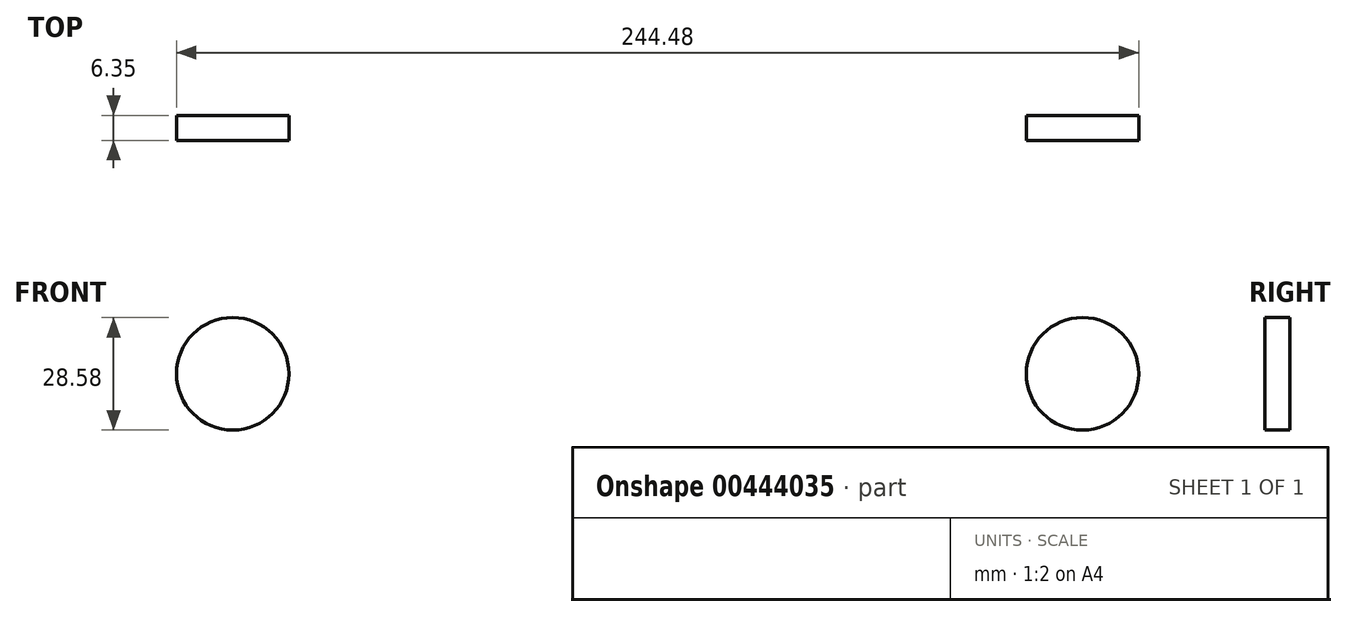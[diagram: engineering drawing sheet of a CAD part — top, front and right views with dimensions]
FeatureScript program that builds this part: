
annotation { "Feature Type Name" : "Feature", "Feature Type Description" : "" }
export const myFeature = defineFeature(function(context is Context, id is Id, definition is map)
    precondition{}
    {
        {
            var Q0;
            Q0=qCreatedBy(makeId("Front.planeOp"),FACE);
            var sketch = newSketch(context, id + "F0", { "sketchPlane" : qUnion([Q0])});
            skLineSegment(sketch, "E0.bottom", {"start": v(215.9, 41.28) * mm, "end": v(-215.9, 41.28) * mm});
            skLineSegment(sketch, "E0.top", {"start": v(215.9, -41.28) * mm, "end": v(-215.9, -41.28) * mm});
            skLineSegment(sketch, "E0.left", {"start": v(215.9, 41.28) * mm, "end": v(215.9, -41.28) * mm});
            skLineSegment(sketch, "E0.right", {"start": v(-215.9, 41.28) * mm, "end": v(-215.9, -41.28) * mm});
            skPoint(sketch, "E0.middle", {"position": v(0, 0) * mm});
            skSolve(sketch);
        }
        {
            var Q0;
            Q0=makeQuery(id+"F0.imprint","IMPRINT",FACE,{"disambiguationData":[TD([[makeQuery(id+"F0.imprint","IMPRINT",EDGE,{"derivedFrom":sQuery(id+"F0.wireOp",EDGE,"E0.bottom")}),1.0]])]});
            extrude(context, id + "F1", {"entities" : qUnion([Q0]), "depth" : 6.35 * mm});
        }
        {
            var Q0;
            Q0=makeQuery(id+"F1.opExtrude","CAP_FACE",FACE,{"disambiguationData":[OSD([sQuery(id+"F0.wireOp",EDGE,"E0.bottom"),sQuery(id+"F0.wireOp",EDGE,"E0.top"),sQuery(id+"F0.wireOp",EDGE,"E0.left"),sQuery(id+"F0.wireOp",EDGE,"E0.right")])],"isStart":false});
            var sketch = newSketch(context, id + "F2", { "sketchPlane" : qUnion([Q0])});
            skLineSegment(sketch, "E1", {"start": v(-215.9, 0) * mm, "end": v(215.9, 0) * mm});
            skCircle(sketch, "E2", {"center": v(107.95, 0) * mm, "radius": 14.29 * mm});
            skCircle(sketch, "E3", {"center": v(-107.95, 0) * mm, "radius": 14.29 * mm});
            skCircle(sketch, "E4", {"center": v(0, 0) * mm, "radius": 14.29 * mm});
            skSolve(sketch);
        }
        {
            var Q0;
            {var subQ0=sQuery(id+"F2.wireOp",EDGE,"E3");var subQ1=sQuery(id+"F2.wireOp",EDGE,"E1");var subQ2=makeQuery(id+"F2.imprint","INTERSECT",VERTEX,{"disambiguationData":[OD(0.0)],"derivedFrom":[subQ1,subQ0]});Q0=makeQuery(id+"F2.imprint","IMPRINT",FACE,{"disambiguationData":[TD([[makeQuery(id+"F2.imprint","IMPRINT",EDGE,{"disambiguationData":[TD([[subQ2,-1.0]])],"derivedFrom":subQ1}),1.0]])]});}
            var Q1;
            {var subQ0=sQuery(id+"F2.wireOp",EDGE,"E3");var subQ1=sQuery(id+"F2.wireOp",EDGE,"E1");var subQ2=makeQuery(id+"F2.imprint","INTERSECT",VERTEX,{"disambiguationData":[OD(0.0)],"derivedFrom":[subQ1,subQ0]});Q1=makeQuery(id+"F2.imprint","IMPRINT",FACE,{"disambiguationData":[TD([[makeQuery(id+"F2.imprint","IMPRINT",EDGE,{"disambiguationData":[TD([[subQ2,-1.0]])],"derivedFrom":subQ1}),-1.0]])]});}
            var Q2;
            {var subQ0=sQuery(id+"F2.wireOp",EDGE,"E4");var subQ1=sQuery(id+"F2.wireOp",EDGE,"E1");var subQ2=makeQuery(id+"F2.imprint","INTERSECT",VERTEX,{"disambiguationData":[OD(0.0)],"derivedFrom":[subQ1,subQ0]});Q2=makeQuery(id+"F2.imprint","IMPRINT",FACE,{"disambiguationData":[TD([[makeQuery(id+"F2.imprint","IMPRINT",EDGE,{"disambiguationData":[TD([[subQ2,-1.0]])],"derivedFrom":subQ1}),-1.0]])]});}
            var Q3;
            {var subQ0=sQuery(id+"F2.wireOp",EDGE,"E4");var subQ1=sQuery(id+"F2.wireOp",EDGE,"E1");var subQ2=makeQuery(id+"F2.imprint","INTERSECT",VERTEX,{"disambiguationData":[OD(0.0)],"derivedFrom":[subQ1,subQ0]});Q3=makeQuery(id+"F2.imprint","IMPRINT",FACE,{"disambiguationData":[TD([[makeQuery(id+"F2.imprint","IMPRINT",EDGE,{"disambiguationData":[TD([[subQ2,-1.0]])],"derivedFrom":subQ1}),1.0]])]});}
            var Q4;
            {var subQ0=sQuery(id+"F2.wireOp",EDGE,"E2");var subQ1=sQuery(id+"F2.wireOp",EDGE,"E1");var subQ2=makeQuery(id+"F2.imprint","INTERSECT",VERTEX,{"disambiguationData":[OD(0.0)],"derivedFrom":[subQ1,subQ0]});Q4=makeQuery(id+"F2.imprint","IMPRINT",FACE,{"disambiguationData":[TD([[makeQuery(id+"F2.imprint","IMPRINT",EDGE,{"disambiguationData":[TD([[subQ2,-1.0]])],"derivedFrom":subQ1}),-1.0]])]});}
            var Q5;
            {var subQ0=sQuery(id+"F2.wireOp",EDGE,"E2");var subQ1=sQuery(id+"F2.wireOp",EDGE,"E1");var subQ2=makeQuery(id+"F2.imprint","INTERSECT",VERTEX,{"disambiguationData":[OD(0.0)],"derivedFrom":[subQ1,subQ0]});Q5=makeQuery(id+"F2.imprint","IMPRINT",FACE,{"disambiguationData":[TD([[makeQuery(id+"F2.imprint","IMPRINT",EDGE,{"disambiguationData":[TD([[subQ2,-1.0]])],"derivedFrom":subQ1}),1.0]])]});}
            var Q6;
            Q6=makeQuery(id+"F1.opExtrude","CAP_FACE",FACE,{"disambiguationData":[OSD([sQuery(id+"F0.wireOp",EDGE,"E0.bottom"),sQuery(id+"F0.wireOp",EDGE,"E0.top"),sQuery(id+"F0.wireOp",EDGE,"E0.left"),sQuery(id+"F0.wireOp",EDGE,"E0.right")])],"isStart":true});
            extrude(context, id + "F3", {"entities" : qUnion([Q0, Q1, Q2, Q3, Q4, Q5]), "operationType" : NewBodyOperationType.REMOVE, "endBound" : BoundingType.UP_TO_SURFACE, "oppositeDirection" : true, "endBoundEntityFace" : qUnion([Q6]), "depth" : 25.4 * mm});
        }
        {
            var Q0;
            Q0=makeQuery(id+"F1.opExtrude","CAP_FACE",FACE,{"disambiguationData":[OSD([sQuery(id+"F0.wireOp",EDGE,"E0.bottom"),sQuery(id+"F0.wireOp",EDGE,"E0.top"),sQuery(id+"F0.wireOp",EDGE,"E0.left"),sQuery(id+"F0.wireOp",EDGE,"E0.right")])],"isStart":false});
            var sketch = newSketch(context, id + "F4", { "sketchPlane" : qUnion([Q0])});
            skLineSegment(sketch, "E5", {"start": v(-107.95, 0) * mm, "end": v(-107.95, 15.16) * mm});
            skLineSegment(sketch, "E6", {"start": v(-107.95, 15.16) * mm, "end": v(-92.8, 15.16) * mm});
            skLineSegment(sketch, "E7", {"start": v(-92.8, 15.16) * mm, "end": v(-92.8, -15.16) * mm});
            skLineSegment(sketch, "E8", {"start": v(-92.8, -15.16) * mm, "end": v(-123.1, -15.16) * mm});
            skLineSegment(sketch, "E9", {"start": v(-123.1, -15.16) * mm, "end": v(-123.1, 15.16) * mm});
            skCircle(sketch, "E10", {"center": v(-92.8, 15.16) * mm, "radius": 2.02 * mm});
            skCircle(sketch, "E11", {"center": v(-92.8, -15.16) * mm, "radius": 2.02 * mm});
            skCircle(sketch, "E12", {"center": v(-123.1, -15.16) * mm, "radius": 2.02 * mm});
            skCircle(sketch, "E13", {"center": v(-123.1, 15.16) * mm, "radius": 2.02 * mm});
            skLineSegment(sketch, "E14", {"start": v(107.95, 0) * mm, "end": v(107.95, 15.16) * mm});
            skLineSegment(sketch, "E15", {"start": v(107.95, 15.16) * mm, "end": v(123.1, 15.16) * mm});
            skLineSegment(sketch, "E16", {"start": v(123.1, 15.16) * mm, "end": v(123.1, -15.16) * mm});
            skLineSegment(sketch, "E17", {"start": v(123.1, -15.16) * mm, "end": v(92.8, -15.16) * mm});
            skLineSegment(sketch, "E18", {"start": v(92.8, -15.16) * mm, "end": v(92.8, 15.16) * mm});
            skCircle(sketch, "E19", {"center": v(123.1, 15.16) * mm, "radius": 2.02 * mm});
            skCircle(sketch, "E20", {"center": v(123.1, -15.16) * mm, "radius": 2.02 * mm});
            skCircle(sketch, "E21", {"center": v(92.8, -15.16) * mm, "radius": 2.02 * mm});
            skCircle(sketch, "E22", {"center": v(92.8, 15.16) * mm, "radius": 2.02 * mm});
            skLineSegment(sketch, "E23", {"start": v(0, 0) * mm, "end": v(0, 15.16) * mm});
            skLineSegment(sketch, "E24", {"start": v(0, 15.16) * mm, "end": v(15.16, 15.16) * mm});
            skLineSegment(sketch, "E25", {"start": v(15.16, 15.16) * mm, "end": v(15.16, -15.16) * mm});
            skLineSegment(sketch, "E26", {"start": v(15.16, -15.16) * mm, "end": v(-15.16, -15.16) * mm});
            skLineSegment(sketch, "E27", {"start": v(-15.16, -15.16) * mm, "end": v(-15.16, 15.16) * mm});
            skCircle(sketch, "E28", {"center": v(15.16, 15.16) * mm, "radius": 2.02 * mm});
            skCircle(sketch, "E29", {"center": v(15.16, -15.16) * mm, "radius": 2.02 * mm});
            skCircle(sketch, "E30", {"center": v(-15.16, -15.16) * mm, "radius": 2.02 * mm});
            skCircle(sketch, "E31", {"center": v(-15.16, 15.16) * mm, "radius": 2.02 * mm});
            skSolve(sketch);
        }
        {
            var Q0;
            {var subQ0=sQuery(id+"F4.wireOp",EDGE,"E8");var subQ1=sQuery(id+"F4.wireOp",EDGE,"E7");var subQ2=makeQuery(id+"F4.imprint","INTERSECT",VERTEX,{"derivedFrom":[subQ1,subQ0]});Q0=makeQuery(id+"F4.imprint","IMPRINT",FACE,{"disambiguationData":[TD([[makeQuery(id+"F4.imprint","IMPRINT",EDGE,{"disambiguationData":[TD([[subQ2,1.0]])],"derivedFrom":subQ1}),1.0]])]});}
            var Q1;
            {var subQ0=sQuery(id+"F4.wireOp",EDGE,"E8");var subQ1=sQuery(id+"F4.wireOp",EDGE,"E7");var subQ2=makeQuery(id+"F4.imprint","INTERSECT",VERTEX,{"derivedFrom":[subQ1,subQ0]});Q1=makeQuery(id+"F4.imprint","IMPRINT",FACE,{"disambiguationData":[TD([[makeQuery(id+"F4.imprint","IMPRINT",EDGE,{"disambiguationData":[TD([[subQ2,1.0]])],"derivedFrom":subQ1}),-1.0]])]});}
            var Q2;
            {var subQ0=sQuery(id+"F4.wireOp",EDGE,"E7");var subQ1=sQuery(id+"F4.wireOp",EDGE,"E6");var subQ2=makeQuery(id+"F4.imprint","INTERSECT",VERTEX,{"derivedFrom":[subQ1,subQ0]});Q2=makeQuery(id+"F4.imprint","IMPRINT",FACE,{"disambiguationData":[TD([[makeQuery(id+"F4.imprint","IMPRINT",EDGE,{"disambiguationData":[TD([[subQ2,1.0]])],"derivedFrom":subQ1}),1.0]])]});}
            var Q3;
            {var subQ0=sQuery(id+"F4.wireOp",EDGE,"E7");var subQ1=sQuery(id+"F4.wireOp",EDGE,"E6");var subQ2=makeQuery(id+"F4.imprint","INTERSECT",VERTEX,{"derivedFrom":[subQ1,subQ0]});Q3=makeQuery(id+"F4.imprint","IMPRINT",FACE,{"disambiguationData":[TD([[makeQuery(id+"F4.imprint","IMPRINT",EDGE,{"disambiguationData":[TD([[subQ2,1.0]])],"derivedFrom":subQ1}),-1.0]])]});}
            var Q4;
            {var subQ0=sQuery(id+"F4.wireOp",EDGE,"E9");var subQ1=sQuery(id+"F4.wireOp",EDGE,"E8");var subQ2=makeQuery(id+"F4.imprint","INTERSECT",VERTEX,{"derivedFrom":[subQ1,subQ0]});Q4=makeQuery(id+"F4.imprint","IMPRINT",FACE,{"disambiguationData":[TD([[makeQuery(id+"F4.imprint","IMPRINT",EDGE,{"disambiguationData":[TD([[subQ2,1.0]])],"derivedFrom":subQ1}),1.0]])]});}
            var Q5;
            {var subQ0=sQuery(id+"F4.wireOp",EDGE,"E9");var subQ1=sQuery(id+"F4.wireOp",EDGE,"E8");var subQ2=makeQuery(id+"F4.imprint","INTERSECT",VERTEX,{"derivedFrom":[subQ1,subQ0]});Q5=makeQuery(id+"F4.imprint","IMPRINT",FACE,{"disambiguationData":[TD([[makeQuery(id+"F4.imprint","IMPRINT",EDGE,{"disambiguationData":[TD([[subQ2,1.0]])],"derivedFrom":subQ1}),-1.0]])]});}
            var Q6;
            Q6=makeQuery(id+"F4.imprint","IMPRINT",FACE,{"disambiguationData":[TD([[makeQuery(id+"F4.imprint","IMPRINT",EDGE,{"derivedFrom":sQuery(id+"F4.wireOp",EDGE,"E13")}),1.0]])]});
            var Q7;
            {var subQ0=sQuery(id+"F4.wireOp",EDGE,"E17");var subQ1=sQuery(id+"F4.wireOp",EDGE,"E16");var subQ2=makeQuery(id+"F4.imprint","INTERSECT",VERTEX,{"derivedFrom":[subQ1,subQ0]});Q7=makeQuery(id+"F4.imprint","IMPRINT",FACE,{"disambiguationData":[TD([[makeQuery(id+"F4.imprint","IMPRINT",EDGE,{"disambiguationData":[TD([[subQ2,1.0]])],"derivedFrom":subQ1}),1.0]])]});}
            var Q8;
            {var subQ0=sQuery(id+"F4.wireOp",EDGE,"E17");var subQ1=sQuery(id+"F4.wireOp",EDGE,"E16");var subQ2=makeQuery(id+"F4.imprint","INTERSECT",VERTEX,{"derivedFrom":[subQ1,subQ0]});Q8=makeQuery(id+"F4.imprint","IMPRINT",FACE,{"disambiguationData":[TD([[makeQuery(id+"F4.imprint","IMPRINT",EDGE,{"disambiguationData":[TD([[subQ2,1.0]])],"derivedFrom":subQ1}),-1.0]])]});}
            var Q9;
            {var subQ0=sQuery(id+"F4.wireOp",EDGE,"E16");var subQ1=sQuery(id+"F4.wireOp",EDGE,"E15");var subQ2=makeQuery(id+"F4.imprint","INTERSECT",VERTEX,{"derivedFrom":[subQ1,subQ0]});Q9=makeQuery(id+"F4.imprint","IMPRINT",FACE,{"disambiguationData":[TD([[makeQuery(id+"F4.imprint","IMPRINT",EDGE,{"disambiguationData":[TD([[subQ2,1.0]])],"derivedFrom":subQ1}),1.0]])]});}
            var Q10;
            {var subQ0=sQuery(id+"F4.wireOp",EDGE,"E16");var subQ1=sQuery(id+"F4.wireOp",EDGE,"E15");var subQ2=makeQuery(id+"F4.imprint","INTERSECT",VERTEX,{"derivedFrom":[subQ1,subQ0]});Q10=makeQuery(id+"F4.imprint","IMPRINT",FACE,{"disambiguationData":[TD([[makeQuery(id+"F4.imprint","IMPRINT",EDGE,{"disambiguationData":[TD([[subQ2,1.0]])],"derivedFrom":subQ1}),-1.0]])]});}
            var Q11;
            Q11=makeQuery(id+"F4.imprint","IMPRINT",FACE,{"disambiguationData":[TD([[makeQuery(id+"F4.imprint","IMPRINT",EDGE,{"derivedFrom":sQuery(id+"F4.wireOp",EDGE,"E22")}),1.0]])]});
            var Q12;
            {var subQ0=sQuery(id+"F4.wireOp",EDGE,"E18");var subQ1=sQuery(id+"F4.wireOp",EDGE,"E17");var subQ2=makeQuery(id+"F4.imprint","INTERSECT",VERTEX,{"derivedFrom":[subQ1,subQ0]});Q12=makeQuery(id+"F4.imprint","IMPRINT",FACE,{"disambiguationData":[TD([[makeQuery(id+"F4.imprint","IMPRINT",EDGE,{"disambiguationData":[TD([[subQ2,1.0]])],"derivedFrom":subQ1}),1.0]])]});}
            var Q13;
            {var subQ0=sQuery(id+"F4.wireOp",EDGE,"E18");var subQ1=sQuery(id+"F4.wireOp",EDGE,"E17");var subQ2=makeQuery(id+"F4.imprint","INTERSECT",VERTEX,{"derivedFrom":[subQ1,subQ0]});Q13=makeQuery(id+"F4.imprint","IMPRINT",FACE,{"disambiguationData":[TD([[makeQuery(id+"F4.imprint","IMPRINT",EDGE,{"disambiguationData":[TD([[subQ2,1.0]])],"derivedFrom":subQ1}),-1.0]])]});}
            var Q14;
            {var subQ0=sQuery(id+"F4.wireOp",EDGE,"E27");var subQ1=sQuery(id+"F4.wireOp",EDGE,"E26");var subQ2=makeQuery(id+"F4.imprint","INTERSECT",VERTEX,{"derivedFrom":[subQ1,subQ0]});Q14=makeQuery(id+"F4.imprint","IMPRINT",FACE,{"disambiguationData":[TD([[makeQuery(id+"F4.imprint","IMPRINT",EDGE,{"disambiguationData":[TD([[subQ2,1.0]])],"derivedFrom":subQ1}),1.0]])]});}
            var Q15;
            {var subQ0=sQuery(id+"F4.wireOp",EDGE,"E27");var subQ1=sQuery(id+"F4.wireOp",EDGE,"E26");var subQ2=makeQuery(id+"F4.imprint","INTERSECT",VERTEX,{"derivedFrom":[subQ1,subQ0]});Q15=makeQuery(id+"F4.imprint","IMPRINT",FACE,{"disambiguationData":[TD([[makeQuery(id+"F4.imprint","IMPRINT",EDGE,{"disambiguationData":[TD([[subQ2,1.0]])],"derivedFrom":subQ1}),-1.0]])]});}
            var Q16;
            {var subQ0=sQuery(id+"F4.wireOp",EDGE,"E26");var subQ1=sQuery(id+"F4.wireOp",EDGE,"E25");var subQ2=makeQuery(id+"F4.imprint","INTERSECT",VERTEX,{"derivedFrom":[subQ1,subQ0]});Q16=makeQuery(id+"F4.imprint","IMPRINT",FACE,{"disambiguationData":[TD([[makeQuery(id+"F4.imprint","IMPRINT",EDGE,{"disambiguationData":[TD([[subQ2,1.0]])],"derivedFrom":subQ1}),1.0]])]});}
            var Q17;
            {var subQ0=sQuery(id+"F4.wireOp",EDGE,"E26");var subQ1=sQuery(id+"F4.wireOp",EDGE,"E25");var subQ2=makeQuery(id+"F4.imprint","INTERSECT",VERTEX,{"derivedFrom":[subQ1,subQ0]});Q17=makeQuery(id+"F4.imprint","IMPRINT",FACE,{"disambiguationData":[TD([[makeQuery(id+"F4.imprint","IMPRINT",EDGE,{"disambiguationData":[TD([[subQ2,1.0]])],"derivedFrom":subQ1}),-1.0]])]});}
            var Q18;
            {var subQ0=sQuery(id+"F4.wireOp",EDGE,"E25");var subQ1=sQuery(id+"F4.wireOp",EDGE,"E24");var subQ2=makeQuery(id+"F4.imprint","INTERSECT",VERTEX,{"derivedFrom":[subQ1,subQ0]});Q18=makeQuery(id+"F4.imprint","IMPRINT",FACE,{"disambiguationData":[TD([[makeQuery(id+"F4.imprint","IMPRINT",EDGE,{"disambiguationData":[TD([[subQ2,1.0]])],"derivedFrom":subQ1}),1.0]])]});}
            var Q19;
            {var subQ0=sQuery(id+"F4.wireOp",EDGE,"E25");var subQ1=sQuery(id+"F4.wireOp",EDGE,"E24");var subQ2=makeQuery(id+"F4.imprint","INTERSECT",VERTEX,{"derivedFrom":[subQ1,subQ0]});Q19=makeQuery(id+"F4.imprint","IMPRINT",FACE,{"disambiguationData":[TD([[makeQuery(id+"F4.imprint","IMPRINT",EDGE,{"disambiguationData":[TD([[subQ2,1.0]])],"derivedFrom":subQ1}),-1.0]])]});}
            var Q20;
            Q20=makeQuery(id+"F4.imprint","IMPRINT",FACE,{"disambiguationData":[TD([[makeQuery(id+"F4.imprint","IMPRINT",EDGE,{"derivedFrom":sQuery(id+"F4.wireOp",EDGE,"E31")}),1.0]])]});
            var Q21;
            Q21=makeQuery(id+"F1.opExtrude","CAP_FACE",FACE,{"disambiguationData":[OSD([sQuery(id+"F0.wireOp",EDGE,"E0.bottom"),sQuery(id+"F0.wireOp",EDGE,"E0.top"),sQuery(id+"F0.wireOp",EDGE,"E0.left"),sQuery(id+"F0.wireOp",EDGE,"E0.right")])],"isStart":true});
            extrude(context, id + "F5", {"entities" : qUnion([Q0, Q1, Q2, Q3, Q4, Q5, Q6, Q7, Q8, Q9, Q10, Q11, Q12, Q13, Q14, Q15, Q16, Q17, Q18, Q19, Q20]), "operationType" : NewBodyOperationType.REMOVE, "endBound" : BoundingType.UP_TO_SURFACE, "oppositeDirection" : true, "endBoundEntityFace" : qUnion([Q21]), "depth" : 25.4 * mm});
        }
    });
